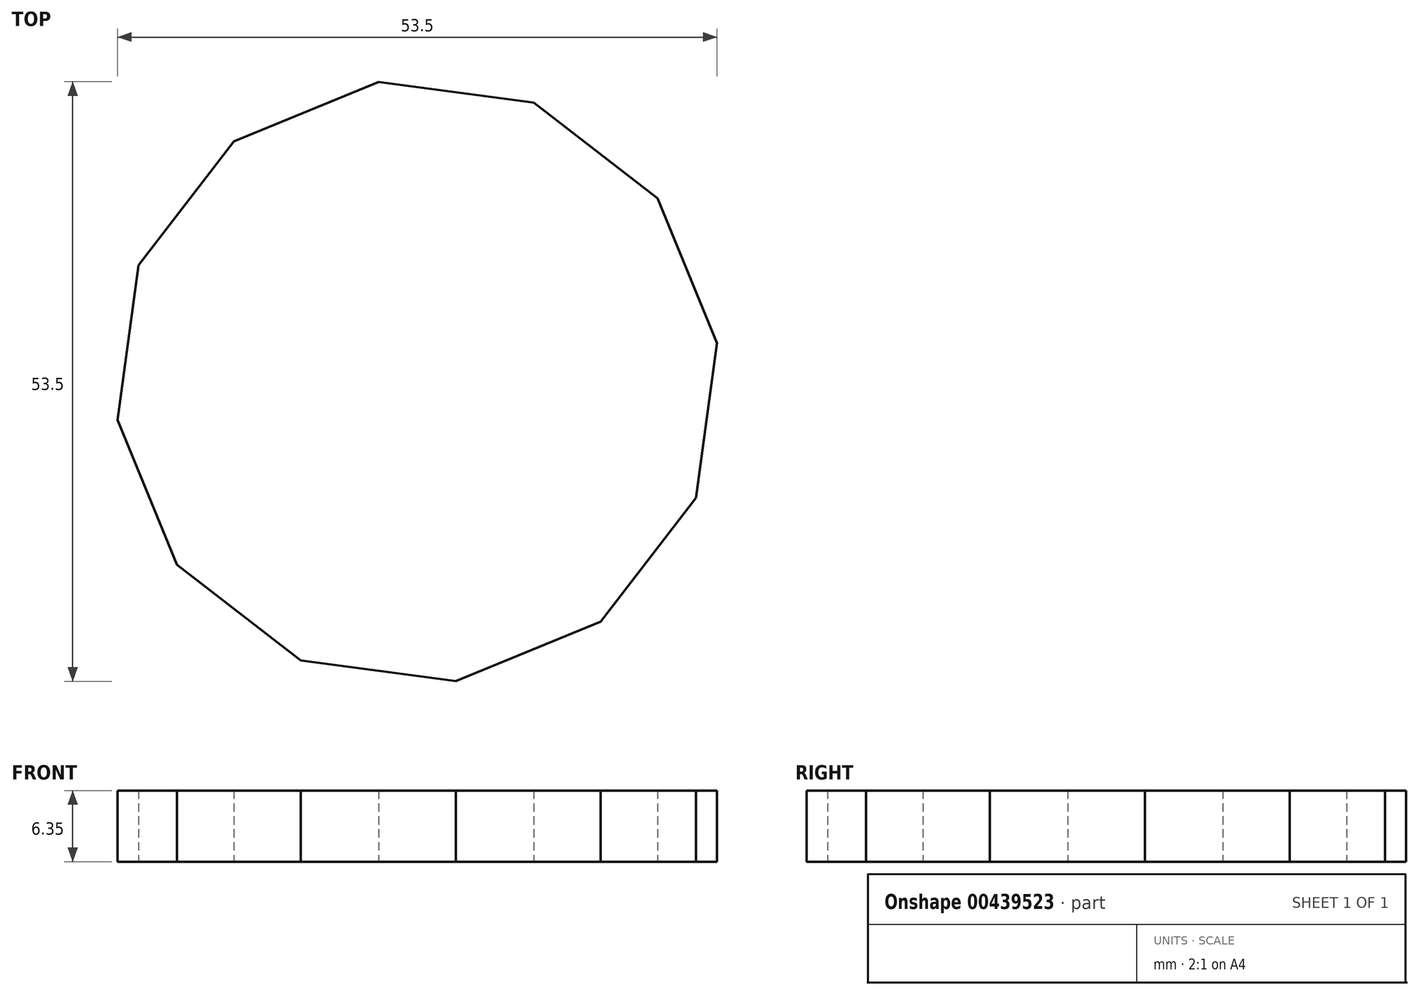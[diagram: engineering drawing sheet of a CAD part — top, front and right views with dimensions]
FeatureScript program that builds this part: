
annotation { "Feature Type Name" : "Feature", "Feature Type Description" : "" }
export const myFeature = defineFeature(function(context is Context, id is Id, definition is map)
    precondition{}
    {
        {
            var Q0;
            Q0=qCreatedBy(makeId("Top.planeOp"),FACE);
            var sketch = newSketch(context, id + "F0", { "sketchPlane" : qUnion([Q0])});
            skCircle(sketch, "E0.cCircle", {"center": v(-5.17, 0) * mm, "radius": 26.05 * mm, "construction": true});
            skLineSegment(sketch, "E0.0", {"start": v(5.22, 24.88) * mm, "end": v(16.27, 16.35) * mm});
            skLineSegment(sketch, "E0.1", {"start": v(16.27, 16.35) * mm, "end": v(21.58, 3.44) * mm});
            skLineSegment(sketch, "E0.2", {"start": v(21.58, 3.44) * mm, "end": v(19.71, -10.4) * mm});
            skLineSegment(sketch, "E0.3", {"start": v(19.71, -10.4) * mm, "end": v(11.18, -21.44) * mm});
            skLineSegment(sketch, "E0.4", {"start": v(11.18, -21.44) * mm, "end": v(-1.73, -26.75) * mm});
            skLineSegment(sketch, "E0.5", {"start": v(-1.73, -26.75) * mm, "end": v(-15.56, -24.88) * mm});
            skLineSegment(sketch, "E0.6", {"start": v(-15.56, -24.88) * mm, "end": v(-26.61, -16.35) * mm});
            skLineSegment(sketch, "E0.7", {"start": v(-26.61, -16.35) * mm, "end": v(-31.92, -3.44) * mm});
            skLineSegment(sketch, "E0.8", {"start": v(-31.92, -3.44) * mm, "end": v(-30.05, 10.4) * mm});
            skLineSegment(sketch, "E0.9", {"start": v(-30.05, 10.4) * mm, "end": v(-21.52, 21.44) * mm});
            skLineSegment(sketch, "E0.10", {"start": v(-21.52, 21.44) * mm, "end": v(-8.61, 26.75) * mm});
            skLineSegment(sketch, "E0.11", {"start": v(-8.61, 26.75) * mm, "end": v(5.22, 24.88) * mm});
            skPoint(sketch, "E0.0.midPoint", {"position": v(10.75, 20.62) * mm});
            skSolve(sketch);
        }
        {
            var Q0;
            Q0=makeQuery(id+"F0.imprint","IMPRINT",FACE,{"disambiguationData":[TD([[makeQuery(id+"F0.imprint","IMPRINT",EDGE,{"derivedFrom":sQuery(id+"F0.wireOp",EDGE,"E0.0")}),-1.0]])]});
            extrude(context, id + "F1", {"entities" : qUnion([Q0]), "depth" : 6.35 * mm});
        }
    });
